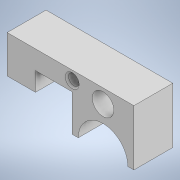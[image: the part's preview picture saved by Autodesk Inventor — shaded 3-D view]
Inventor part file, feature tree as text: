
AUTODESK INVENTOR PART (.ipt)
format: ipt  version: 2022 (Build 260153000, 153)  size: 113,152 bytes
history: native  units: in
note: dims shown in document units (in); Inventor stores cm internally (conversion verified against a paired STEP export)
features: sketch x2, extrude x1, hole x1
ambient origin geometry x8: Origin, YZ Plane, XZ Plane, XY Plane, X Axis, Y Axis, Z Axis, Center Point
bodies: Solid1 (feature_tree)
feature tree (4):
  extrude  "Extrusion1"  [1 undecoded]
  hole  "Hole1"  [1 undecoded]
  sketch  "Sketch1"  dims[d0=0.2505in d1=0.0in]
  sketch  "Sketch3"  dims[d7=0.07in d8=0.75in d9=0.09in d10=0.25in d11=0.5635in d12=1.0in d13=0.8108in]
note: 2 required parameter values undecoded (feature->parameter linkage not recoverable at this tier; creation-order binding heuristic only, values carry confidence <= 0.55)
